# Revit family: AFX-Sia-LED_Sconce-1
name_source: partatom
category: Lighting Fixtures
units: mm (PartAtom-declared; Revit-internal decimal feet)

## family parameters
Cut with Voids When Loaded = No
Host = Face
Light Source = Yes
Part Type = Normal
Room Calculation Point = No
Round Connector Dimension = Use Diameter
Shared = No

## types (1)
- SIAS0717LAJUDBK
    Apparent Load = 0 VA
    Assembly Code = D5020200
    Body Finish = AFX - Black Steel
    Color Filter = 16777215
    Colour Rendering Index = 80
    Default Elevation = 48"
    Depth = 4"
    Description = LED Sconce - 16 3/4"H x 6 3/4"W x 4"D
    Diffuser Finish = AFX - White Acrylic
    Dimming Lamp Color Temperature Shift = <None>
    Emit Shape Visible in Rendering = No
    Emit from Rectangle Length = 5"
    Emit from Rectangle Width = 16"
    Height = 16 3/4"
    Housing Finish = AFX - Black Steel
    Keynote = 12500
    Manufacturer = AFX Inc
    Model = SIAS0717LAJUDBK
    Photometric Web File = SIAS0717LAJUDSN_3000K_IES.IES
    Product Documentation Link = https://www.afxinc.com
    Revit File Built By = https://servex-us.com
    Sustainability = https://lamprecycle.org
    Tilt Angle = 0.00°
    Type Comments = Sia
    URL = https://www.afxinc.com
    Voltage = 120 V
    Wattage Comments = 25W
    Width = 6 3/4"

## geometry (parser evidence)
native form markers: Sweep x4
no freeform markers — native parametric forms only
